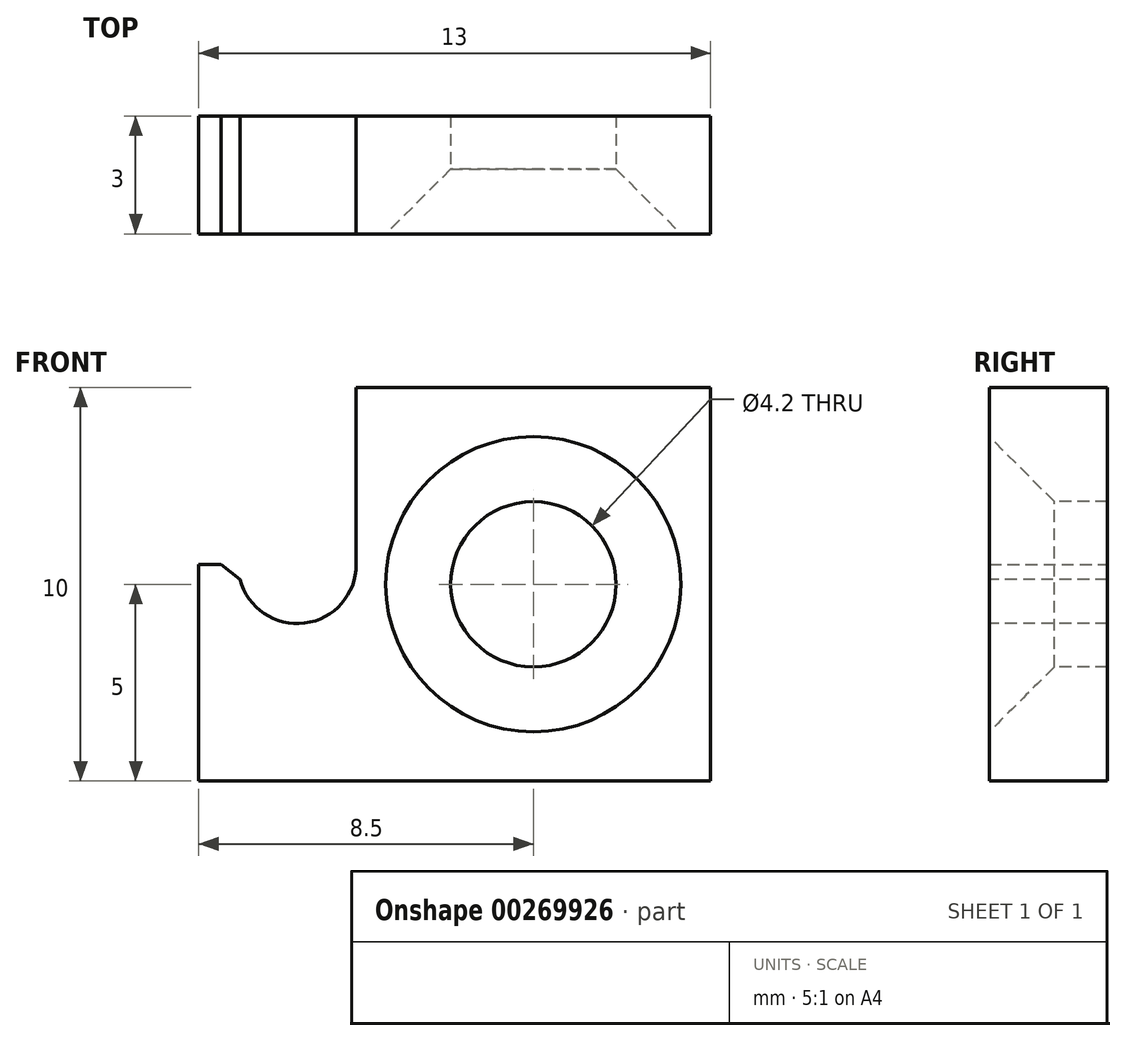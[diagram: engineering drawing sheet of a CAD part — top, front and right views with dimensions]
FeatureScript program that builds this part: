
annotation { "Feature Type Name" : "Feature", "Feature Type Description" : "" }
export const myFeature = defineFeature(function(context is Context, id is Id, definition is map)
    precondition{}
    {
        {
            var Q0;
            Q0=qCreatedBy(makeId("Front.planeOp"),FACE);
            var sketch = newSketch(context, id + "F0", { "sketchPlane" : qUnion([Q0])});
            skLineSegment(sketch, "E0.bottom", {"start": v(0, 0) * mm, "end": v(-13, 0) * mm});
            skLineSegment(sketch, "E0.top", {"start": v(0, 10) * mm, "end": v(-9, 10) * mm});
            skLineSegment(sketch, "E0.left", {"start": v(0, 0) * mm, "end": v(0, 10) * mm});
            skLineSegment(sketch, "E0.right", {"start": v(-13, 0) * mm, "end": v(-13, 5.5) * mm});
            skLineSegment(sketch, "E1.top", {"start": v(-13, 5.5) * mm, "end": v(-12, 5.5) * mm});
            skLineSegment(sketch, "E1.right", {"start": v(-9, 10) * mm, "end": v(-9, 5.5) * mm});
            skArc(sketch, "E2", {"start": v(-12, 5.5) * mm, "mid": v(-10.5, 4) * mm, "end": v(-9, 5.5) * mm});
            skSolve(sketch);
        }
        {
            var Q0;
            Q0 = qSketchRegion(id + "F0", true);
            extrude(context, id + "F1", {"entities" : qUnion([Q0]), "oppositeDirection" : true, "depth" : 3 * mm});
        }
        {
            var Q0;
            Q0=makeQuery(id+"F1.opExtrude","CAP_FACE",FACE,{"disambiguationData":[OSD([sQuery(id+"F0.wireOp",EDGE,"E0.bottom"),sQuery(id+"F0.wireOp",EDGE,"E0.top"),sQuery(id+"F0.wireOp",EDGE,"E0.left"),sQuery(id+"F0.wireOp",EDGE,"E0.right"),sQuery(id+"F0.wireOp",EDGE,"E1.top"),sQuery(id+"F0.wireOp",EDGE,"E1.right"),sQuery(id+"F0.wireOp",EDGE,"E2")])],"isStart":true});
            var sketch = newSketch(context, id + "F2", { "sketchPlane" : qUnion([Q0])});
            skPoint(sketch, "E3", {"position": v(-4.5, 5) * mm});
            skSolve(sketch);
        }
        {
            var Q0;
            Q0=sQuery(id+"F2.wireOp",VERTEX,"E3");
            var Q1;
            Q1=makeQuery(id+"F1.opExtrude","SWEPT_BODY",BODY,{"disambiguationData":[OSD([sQuery(id+"F0.wireOp",EDGE,"E0.bottom"),sQuery(id+"F0.wireOp",EDGE,"E0.top"),sQuery(id+"F0.wireOp",EDGE,"E0.left"),sQuery(id+"F0.wireOp",EDGE,"E0.right"),sQuery(id+"F0.wireOp",EDGE,"E1.top"),sQuery(id+"F0.wireOp",EDGE,"E1.right"),sQuery(id+"F0.wireOp",EDGE,"E2")])]});
            hole(context, id + "F3", {"style" : HoleStyle.C_SINK, "endStyle" : HoleEndStyle.THROUGH, "holeDiameter" : 4.2 * mm, "cSinkDiameter" : 7.5 * mm, "cSinkAngle" : 90 * degree, "tappedDepth" : 6 * mm, "tapClearance" : 2, "locations" : qUnion([Q0]), "scope" : qUnion([Q1])});
        }
        {
            var Q0;
            Q0=makeQuery(id+"F1.opExtrude","SWEPT_EDGE",EDGE,{"disambiguationData":[OSD([sQuery(id+"F0.wireOp",EDGE,"E1.top"),sQuery(id+"F0.wireOp",EDGE,"E2")])]});
            chamfer(context, id + "F4", {"entities" : qUnion([Q0]), "width" : .5 * mm, "tangentPropagation" : true});
        }
    });
